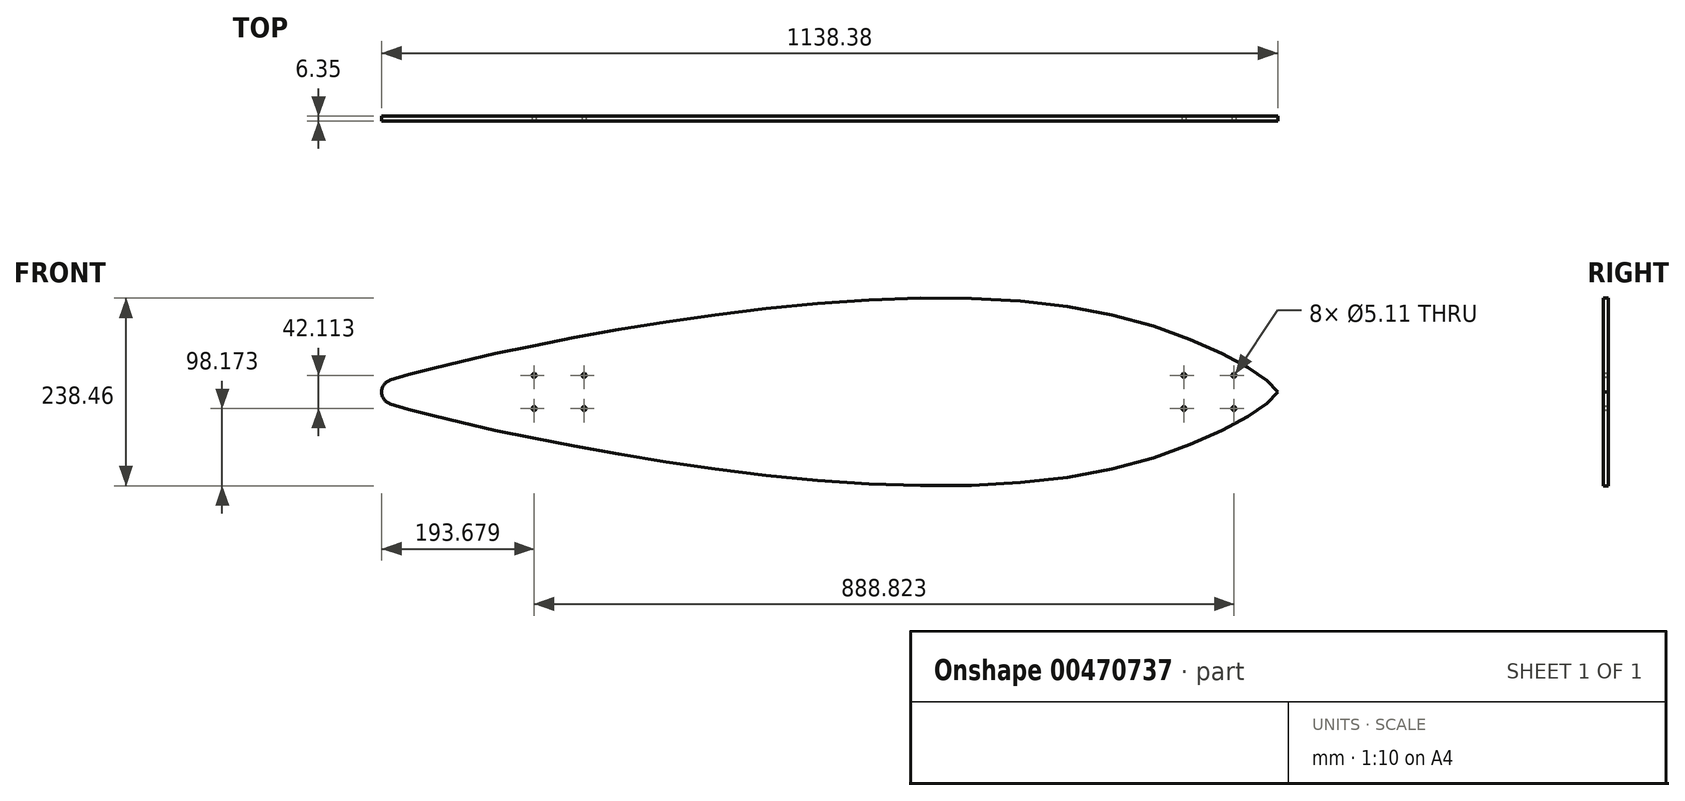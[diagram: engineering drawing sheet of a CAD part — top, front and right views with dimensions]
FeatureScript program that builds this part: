
annotation { "Feature Type Name" : "Feature", "Feature Type Description" : "" }
export const myFeature = defineFeature(function(context is Context, id is Id, definition is map)
    precondition{}
    {
        {
            var Q0;
            Q0=qCreatedBy(makeId("Front.planeOp"),FACE);
            var sketch = newSketch(context, id + "F0", { "sketchPlane" : qUnion([Q0])});
            skArc(sketch, "E0", {"start": v(29.98, 142.11) * mm, "mid": v(22.01, 136.35) * mm, "end": v(18.96, 127) * mm});
            skFitSpline(sketch, "E1", {"points": [v(29.98, 142.11) * mm, v(299.8, 202.51) * mm, v(929.07, 228.6) * mm, v(1157.34, 127) * mm], "startDerivative": vector(444.7, 142.96) * mm, "endDerivative": vector(202.03, -293.2) * mm});
            skLineSegment(sketch, "E2", {"start": v(18.96, 127) * mm, "end": v(1157.34, 127) * mm, "construction": true});
            skArc(sketch, "E3", {"start": v(18.96, 127) * mm, "mid": v(22.01, 117.65) * mm, "end": v(29.98, 111.89) * mm});
            skFitSpline(sketch, "E4", {"points": [v(29.98, 111.89) * mm, v(299.8, 51.49) * mm, v(929.07, 25.4) * mm, v(1157.34, 127) * mm], "startDerivative": vector(444.7, -142.96) * mm, "endDerivative": vector(202.03, 293.2) * mm});
            skSolve(sketch);
        }
        {
            var Q0;
            Q0 = qSketchRegion(id + "F0", true);
            extrude(context, id + "F1", {"entities" : qUnion([Q0]), "depth" : 6.35 * mm});
        }
        {
            var Q0;
            Q0=makeQuery(id+"F1.opExtrude","CAP_FACE",FACE,{"disambiguationData":[OSD([sQuery(id+"F0.wireOp",EDGE,"E0"),sQuery(id+"F0.wireOp",EDGE,"E1"),sQuery(id+"F0.wireOp",EDGE,"E3"),sQuery(id+"F0.wireOp",EDGE,"E4")])],"isStart":false});
            var sketch = newSketch(context, id + "F2", { "sketchPlane" : qUnion([Q0])});
            skPoint(sketch, "E5", {"position": v(212.64, 148.06) * mm});
            skPoint(sketch, "E6", {"position": v(276.14, 148.06) * mm});
            skPoint(sketch, "E7", {"position": v(276.14, 105.94) * mm});
            skPoint(sketch, "E8", {"position": v(212.64, 105.94) * mm});
            skLineSegment(sketch, "E9", {"start": v(212.64, 105.94) * mm, "end": v(212.64, 148.06) * mm, "construction": true});
            skLineSegment(sketch, "E10", {"start": v(276.14, 148.06) * mm, "end": v(212.64, 148.06) * mm, "construction": true});
            skLineSegment(sketch, "E11", {"start": v(276.14, 148.06) * mm, "end": v(276.14, 105.94) * mm, "construction": true});
            skLineSegment(sketch, "E12", {"start": v(276.14, 105.94) * mm, "end": v(212.64, 105.94) * mm, "construction": true});
            skLineSegment(sketch, "E13", {"start": v(34.84, 127) * mm, "end": v(212.64, 127) * mm, "construction": true});
            skPoint(sketch, "E14", {"position": v(1037.96, 148.06) * mm});
            skPoint(sketch, "E15", {"position": v(1101.46, 148.06) * mm});
            skPoint(sketch, "E16", {"position": v(1101.46, 105.94) * mm});
            skPoint(sketch, "E17", {"position": v(1037.96, 105.94) * mm});
            skLineSegment(sketch, "E18", {"start": v(1037.96, 148.06) * mm, "end": v(1101.46, 148.06) * mm, "construction": true});
            skLineSegment(sketch, "E19", {"start": v(1101.46, 148.06) * mm, "end": v(1101.46, 105.94) * mm, "construction": true});
            skLineSegment(sketch, "E20", {"start": v(1101.46, 105.94) * mm, "end": v(1037.96, 105.94) * mm, "construction": true});
            skLineSegment(sketch, "E21", {"start": v(1037.96, 105.94) * mm, "end": v(1037.96, 148.06) * mm, "construction": true});
            skSolve(sketch);
        }
        {
            var Q0;
            Q0=sQuery(id+"F2.wireOp",VERTEX,"E6");
            var Q1;
            Q1=sQuery(id+"F2.wireOp",VERTEX,"E7");
            var Q2;
            Q2=sQuery(id+"F2.wireOp",VERTEX,"E5");
            var Q3;
            Q3=sQuery(id+"F2.wireOp",VERTEX,"E14");
            var Q4;
            Q4=sQuery(id+"F2.wireOp",VERTEX,"E17");
            var Q5;
            Q5=sQuery(id+"F2.wireOp",VERTEX,"E16");
            var Q6;
            Q6=sQuery(id+"F2.wireOp",VERTEX,"E15");
            var Q7;
            Q7=sQuery(id+"F2.wireOp",VERTEX,"E8");
            var Q8;
            Q8=makeQuery(id+"F1.opExtrude","SWEPT_BODY",BODY,{"disambiguationData":[OSD([sQuery(id+"F0.wireOp",EDGE,"E0"),sQuery(id+"F0.wireOp",EDGE,"E1"),sQuery(id+"F0.wireOp",EDGE,"E3"),sQuery(id+"F0.wireOp",EDGE,"E4")])]});
            hole(context, id + "F3", {"style" : HoleStyle.SIMPLE, "endStyle" : HoleEndStyle.THROUGH, "holeDiameter" : 5.1 * mm, "isTappedThrough" : true, "tappedDepth" : 12.7 * mm, "tapClearance" : 3, "locations" : qUnion([Q0, Q1, Q2, Q3, Q4, Q5, Q6, Q7]), "scope" : qUnion([Q8])});
        }
    });
